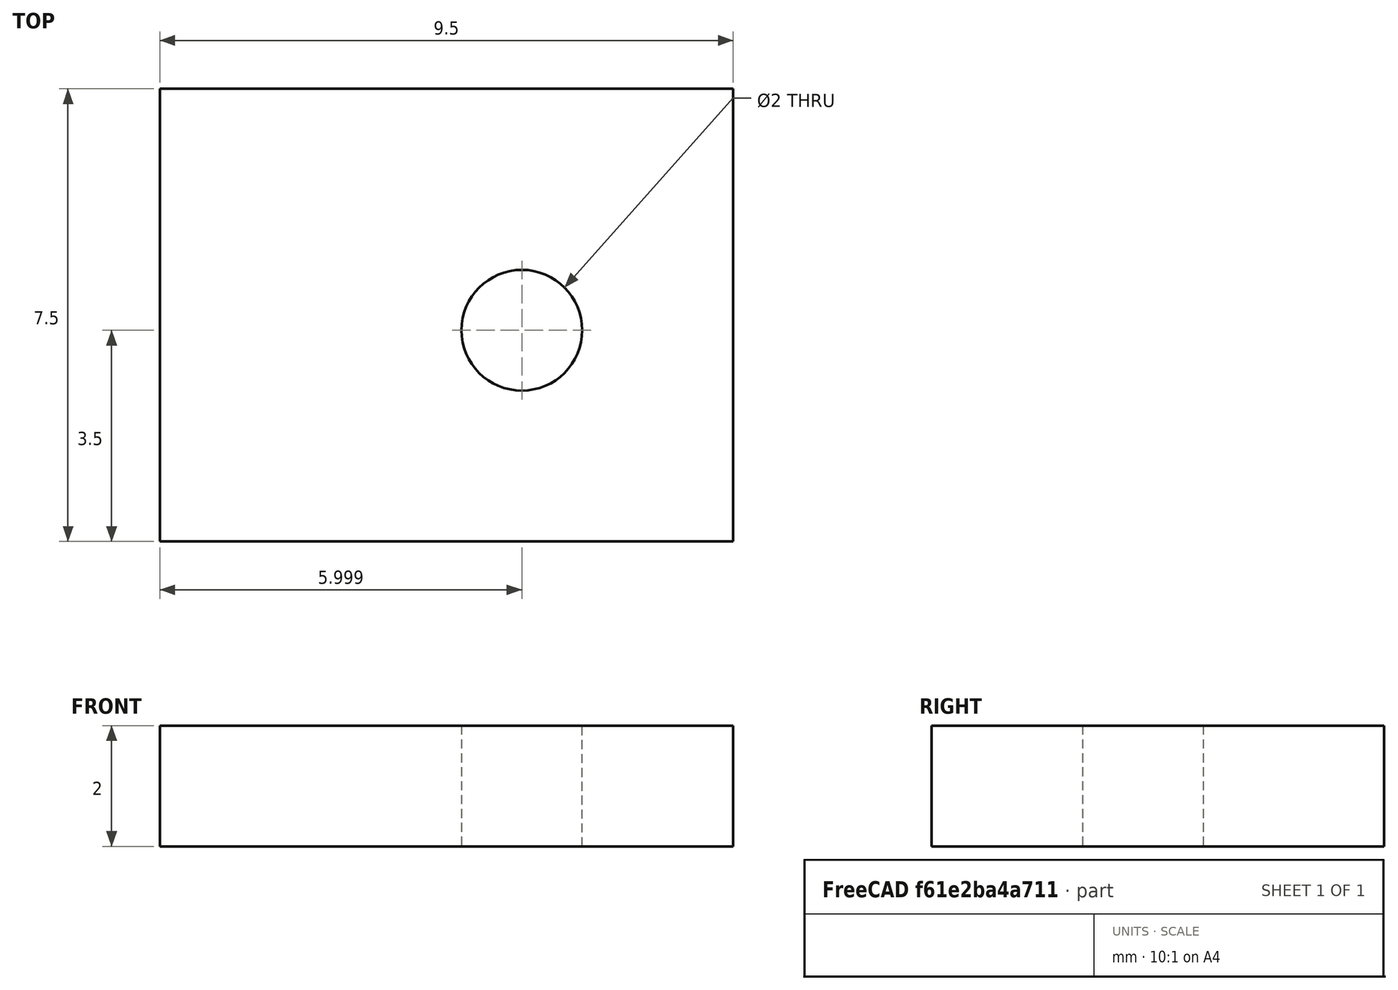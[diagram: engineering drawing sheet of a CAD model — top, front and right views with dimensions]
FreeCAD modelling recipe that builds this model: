
FCSTD DOCUMENT  (FreeCAD 1.0R39109 (Git))
Label: padding_for_ush_9.5x7.5x2
License: All rights reserved
LicenseURL: https://en.wikipedia.org/wiki/All_rights_reserved
objects: Sketcher::SketchObject×1, PartDesign::Pad×1, PartDesign::Body×1
note: 6 computed .brp shape members not serialized (recipe doc carries the construction recipe); baked Part::Feature solids carry a one-line shape summary decoded from their .brp

FEATURE [Sketcher::SketchObject] Sketch
  ArcFitTolerance = 1e-06
  AttachmentSupport = -> [XY_Plane]
  FullyConstrained = false
  MakeInternals = false
  MapMode = 5
  sketch-geometry (5):
    g0: LineSegment StartX=0 StartY=0 StartZ=0 EndX=9.5 EndY=0 EndZ=0
    g1: LineSegment StartX=9.5 StartY=0 StartZ=0 EndX=9.5 EndY=7.5 EndZ=0
    g2: LineSegment StartX=9.5 StartY=7.5 StartZ=0 EndX=0 EndY=7.5 EndZ=0
    g3: LineSegment StartX=0 StartY=7.5 StartZ=0 EndX=0 EndY=0 EndZ=0
    g4: Circle CenterX=5.99935 CenterY=3.49977 CenterZ=0 NormalX=0 NormalY=0 NormalZ=1 AngleXU=0 Radius=1
  constraints (12):
    c: Coincident(g0,g1)
    c: Coincident(g1,g2)
    c: Coincident(g2,g3)
    c: Coincident(g3,g0)
    c: Horizontal(g0)
    c: Horizontal(g2)
    c: Vertical(g1)
    c: Vertical(g3)
    c: Distance(g1,g3) = 9.5
    c: Distance(g0,g2) = 7.5
    c: Coincident(g0,g-1)
    c: Diameter(g4) = 2
FEATURE [PartDesign::Pad] Pad
  Direction = (0,0,1)
  Length = 2
  Length2 = 10
  Profile = -> Sketch
  ReferenceAxis = -> Sketch [N_Axis]
  Refine = true
  Suppressed = false
  Type = 0
FEATURE [PartDesign::Body] Body
  AllowCompound = false
  Group = -> [Sketch,Pad]
  Origin = -> Origin
  Tip = -> Pad
